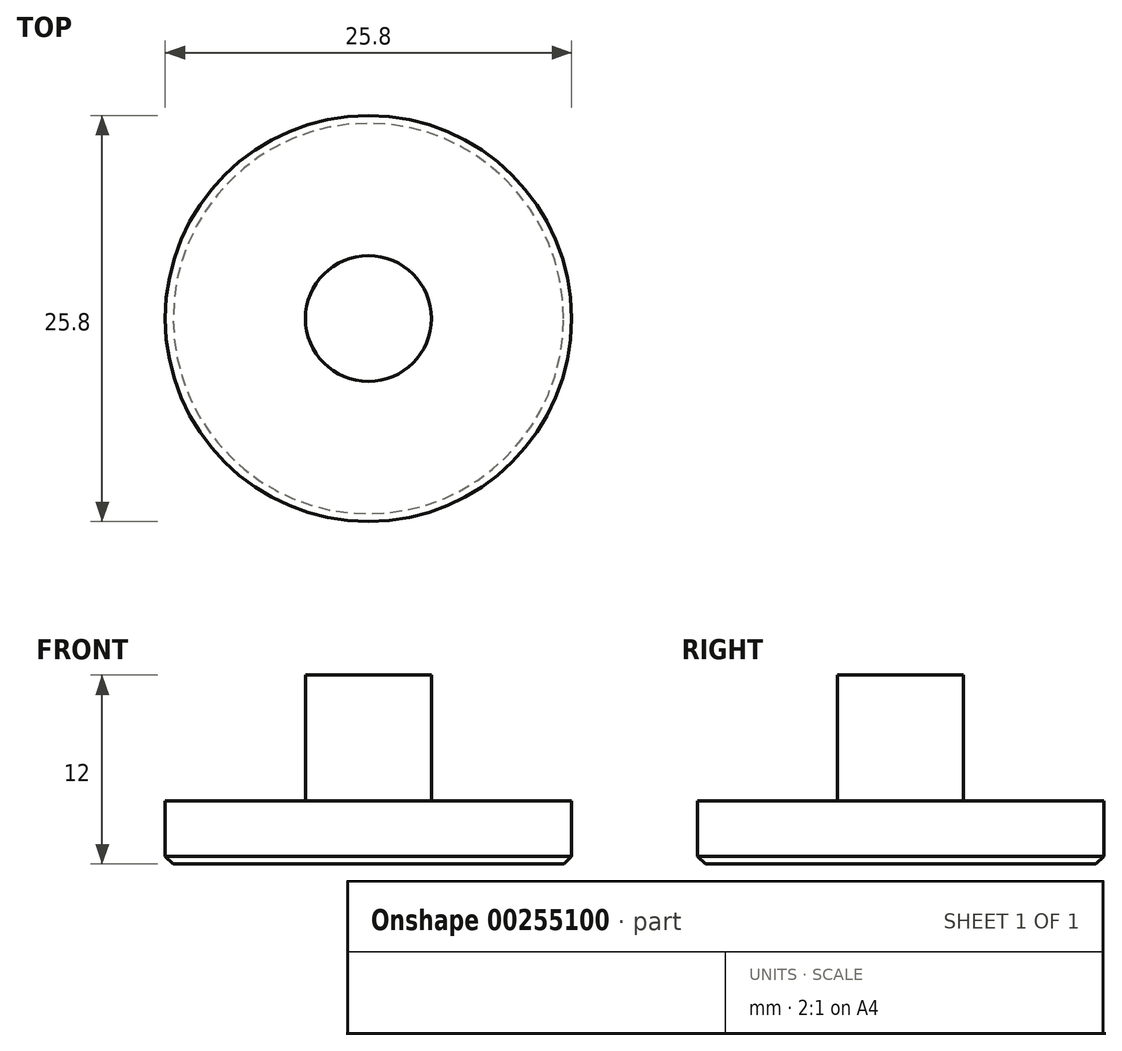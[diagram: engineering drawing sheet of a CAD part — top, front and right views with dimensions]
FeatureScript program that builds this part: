
annotation { "Feature Type Name" : "Feature", "Feature Type Description" : "" }
export const myFeature = defineFeature(function(context is Context, id is Id, definition is map)
    precondition{}
    {
        {
            var Q0;
            Q0=qCreatedBy(makeId("Top.planeOp"),FACE);
            var sketch = newSketch(context, id + "F0", { "sketchPlane" : qUnion([Q0])});
            skCircle(sketch, "E0", {"center": v(0, 0) * mm, "radius": 12.9 * mm});
            skSolve(sketch);
        }
        {
            var Q0;
            Q0=makeQuery(id+"F0.imprint","IMPRINT",FACE,{"disambiguationData":[TD([[makeQuery(id+"F0.imprint","IMPRINT",EDGE,{"derivedFrom":sQuery(id+"F0.wireOp",EDGE,"E0")}),1.0]])]});
            extrude(context, id + "F1", {"entities" : qUnion([Q0]), "depth" : 4 * mm});
        }
        {
            var Q0;
            Q0=makeQuery(id+"F1.opExtrude","CAP_FACE",FACE,{"disambiguationData":[OSD([sQuery(id+"F0.wireOp",EDGE,"E0")])],"isStart":false});
            var sketch = newSketch(context, id + "F2", { "sketchPlane" : qUnion([Q0])});
            skCircle(sketch, "E1", {"center": v(0, 0) * mm, "radius": 4 * mm});
            skSolve(sketch);
        }
        {
            var Q0;
            Q0=makeQuery(id+"F2.imprint","IMPRINT",FACE,{"disambiguationData":[TD([[makeQuery(id+"F2.imprint","IMPRINT",EDGE,{"derivedFrom":sQuery(id+"F2.wireOp",EDGE,"E1")}),1.0]])]});
            extrude(context, id + "F3", {"entities" : qUnion([Q0]), "operationType" : NewBodyOperationType.ADD, "depth" : 8 * mm});
        }
        {
            var Q0;
            Q0=makeQuery(id+"F1.opExtrude","CAP_EDGE",EDGE,{"disambiguationData":[OSD([sQuery(id+"F0.wireOp",EDGE,"E0")])],"isStart":true});
            chamfer(context, id + "F4", {"entities" : qUnion([Q0]), "width" : 0.5 * mm, "tangentPropagation" : true});
        }
    });
